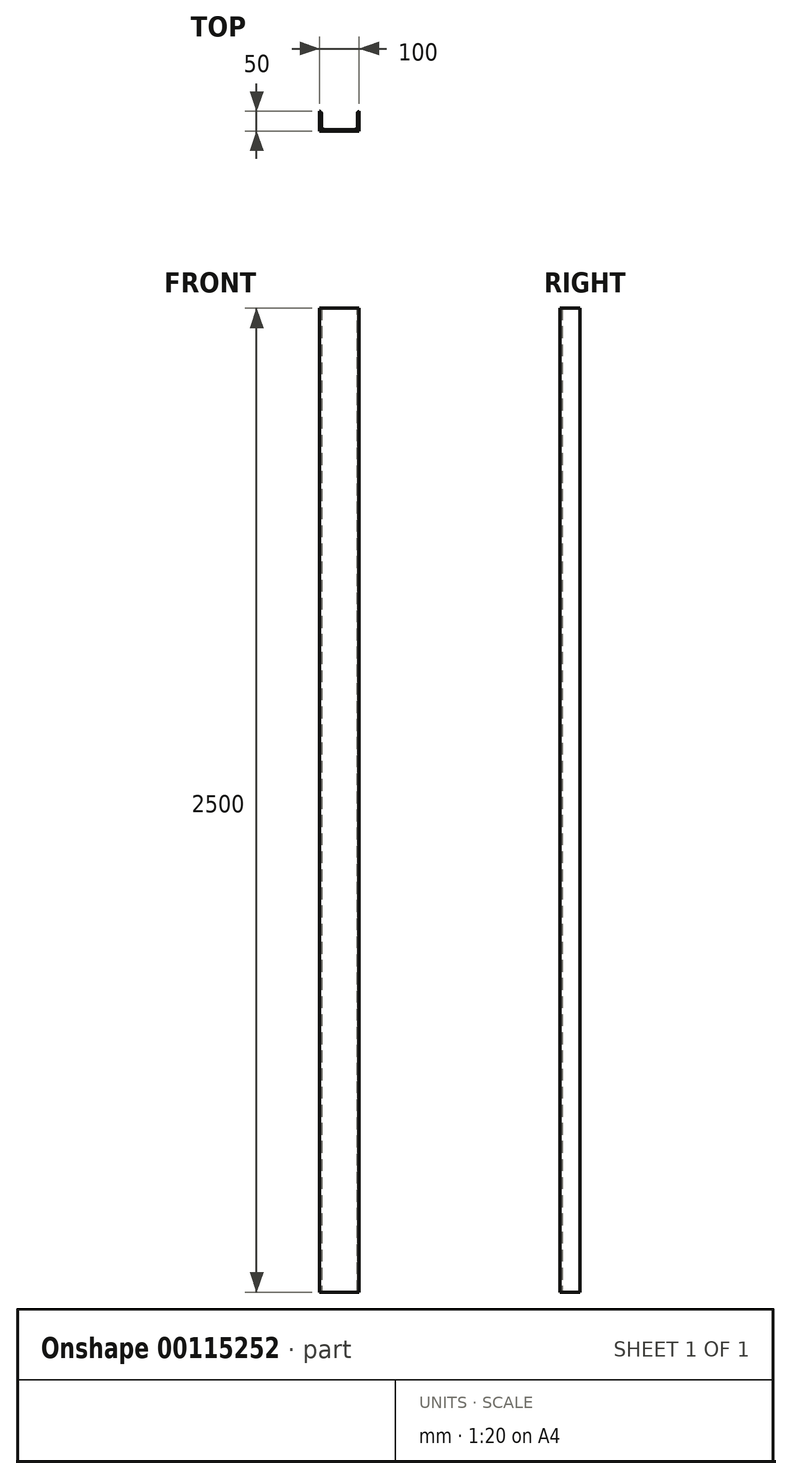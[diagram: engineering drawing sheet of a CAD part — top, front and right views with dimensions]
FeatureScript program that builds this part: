
annotation { "Feature Type Name" : "Feature", "Feature Type Description" : "" }
export const myFeature = defineFeature(function(context is Context, id is Id, definition is map)
    precondition{}
    {
        {
            var Q0;
            Q0=qCreatedBy(makeId("Top.planeOp"),FACE);
            var sketch = newSketch(context, id + "F0", { "sketchPlane" : qUnion([Q0])});
            skLineSegment(sketch, "E0.bottom", {"start": v(50, -25) * mm, "end": v(-50, -25) * mm});
            skLineSegment(sketch, "E0.top", {"start": v(50, 25) * mm, "end": v(46, 25) * mm});
            skLineSegment(sketch, "E0.left", {"start": v(50, -25) * mm, "end": v(50, 25) * mm});
            skLineSegment(sketch, "E0.right", {"start": v(-50, -25) * mm, "end": v(-50, 25) * mm});
            skPoint(sketch, "E0.middle", {"position": v(0, 0) * mm});
            skLineSegment(sketch, "E1.0", {"start": v(-46, -21) * mm, "end": v(-46, 25) * mm});
            skLineSegment(sketch, "E1.1", {"start": v(46, -21) * mm, "end": v(-46, -21) * mm});
            skLineSegment(sketch, "E1.2", {"start": v(46, -21) * mm, "end": v(46, 25) * mm});
            skLineSegment(sketch, "E2.trimOffspring", {"start": v(-46, 25) * mm, "end": v(-50, 25) * mm});
            skSolve(sketch);
        }
        {
            var Q0;
            Q0 = qSketchRegion(id + "F0", true);
            extrude(context, id + "F1", {"entities" : qUnion([Q0]), "depth" : 2500 * mm});
        }
        {
            var Q0;
            Q0=makeQuery(id+"F1.opExtrude","SWEPT_EDGE",EDGE,{"disambiguationData":[OSD([sQuery(id+"F0.wireOp",EDGE,"E1.1"),sQuery(id+"F0.wireOp",EDGE,"E1.2")])]});
            var Q1;
            Q1=makeQuery(id+"F1.opExtrude","SWEPT_EDGE",EDGE,{"disambiguationData":[OSD([sQuery(id+"F0.wireOp",EDGE,"E1.0"),sQuery(id+"F0.wireOp",EDGE,"E1.1")])]});
            fillet(context, id + "F2", {"entities" : qUnion([Q0, Q1]), "radius" : 10 * mm, "tangentPropagation" : true, "rho" : 0.5, "crossSection" : FilletCrossSection.CONIC, "allowEdgeOverflow" : false});
        }
        {
            var Q0;
            Q0=makeQuery(id+"F1.opExtrude","SWEPT_EDGE",EDGE,{"disambiguationData":[OSD([sQuery(id+"F0.wireOp",EDGE,"E1.0"),sQuery(id+"F0.wireOp",EDGE,"E2.trimOffspring")])]});
            var Q1;
            Q1=makeQuery(id+"F1.opExtrude","SWEPT_EDGE",EDGE,{"disambiguationData":[OSD([sQuery(id+"F0.wireOp",EDGE,"E0.top"),sQuery(id+"F0.wireOp",EDGE,"E1.2")])]});
            fillet(context, id + "F3", {"entities" : qUnion([Q0, Q1]), "radius" : 4 * mm, "tangentPropagation" : true, "allowEdgeOverflow" : false});
        }
    });
